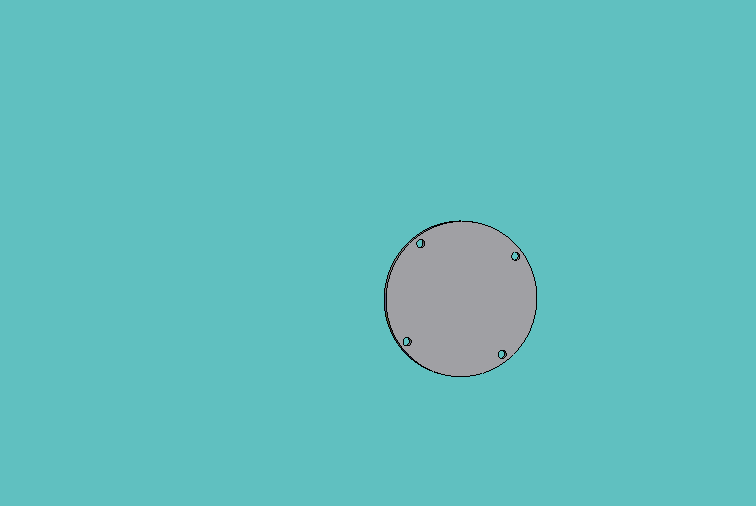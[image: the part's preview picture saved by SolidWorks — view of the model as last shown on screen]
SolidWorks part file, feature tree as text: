
SOLIDWORKS PART (.sldprt)
format: sldprt  version: not decoded by parser v0  size: 226,816 bytes
history: native  units: mm
features: sketch x3, material x1, extrude x1, hole x1 (+12 scaffold rows collapsed)
feature tree (18):
  scaffold x12  (default folders/planes/origin — collapsed)
  material  "Material <not specified>"
  sketch  "Sketch1"  dims[D1=100.0mm]
  extrude  "Extrude1"  Depth=5mm
  hole  "M5.5 (5.5) Diameter Hole2"  Diameter=5.5mm Depth=5mm
  sketch  "Sketch5"  dims[c1.D1=90.0mm c1.D2=~63.573419mm c2.D2=90.0deg c3.D2=~63.573419mm c3.D3=~63.705733mm c4.D2=~75.429122mm c4.D3=~49.092326mm]
  sketch  "Sketch4"  dims[hole-wizard template sketch: 60 standard entries collapsed; hole parameters kept: c18.Thru Hole Depth=5.0mm]
decode coverage: 5 of 5 modeling features carry decoded parameters
note: ~ marks probable driven/reference dimensions
note: suppression state not decoded; provenance and decode notes live in map.json
